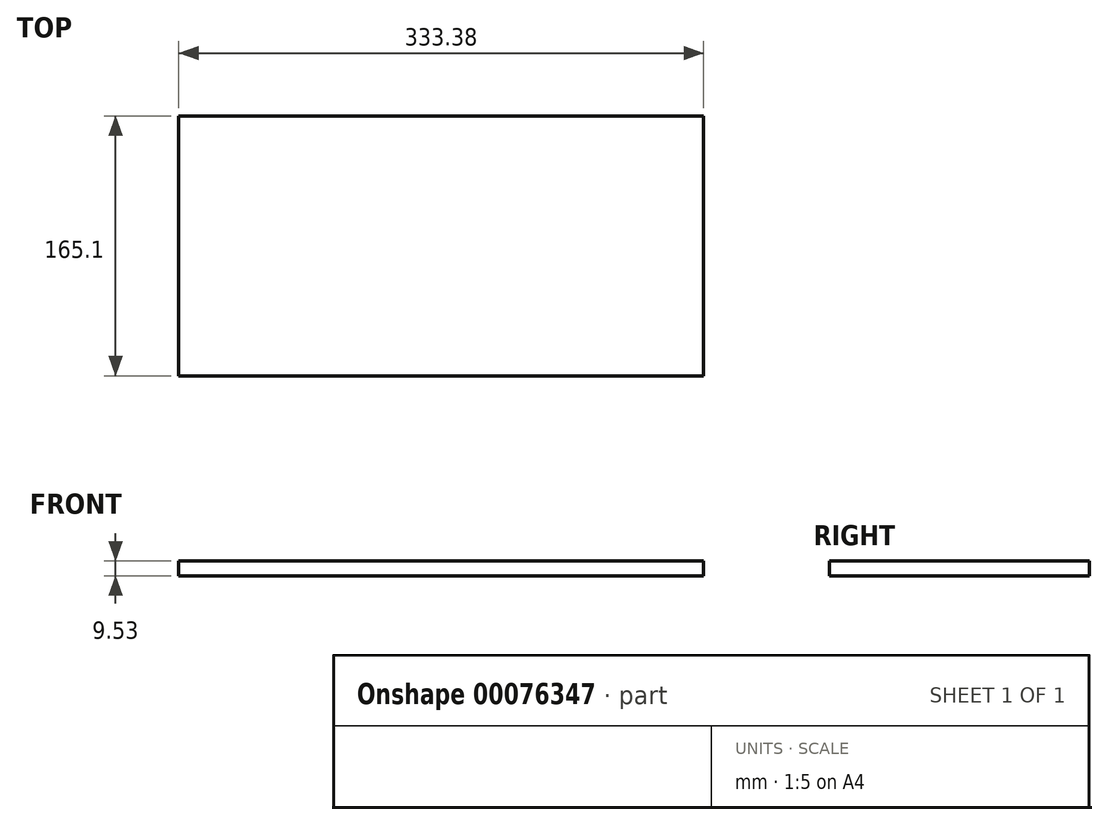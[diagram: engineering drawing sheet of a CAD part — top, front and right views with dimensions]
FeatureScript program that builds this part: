
annotation { "Feature Type Name" : "Feature", "Feature Type Description" : "" }
export const myFeature = defineFeature(function(context is Context, id is Id, definition is map)
    precondition{}
    {
        {
            var Q0;
            Q0=qCreatedBy(makeId("Top.planeOp"),FACE);
            var sketch = newSketch(context, id + "F0", { "sketchPlane" : qUnion([Q0])});
            skLineSegment(sketch, "E0.bottom", {"start": v(166.69, 82.55) * mm, "end": v(-166.69, 82.55) * mm});
            skLineSegment(sketch, "E0.top", {"start": v(166.69, -82.55) * mm, "end": v(-166.69, -82.55) * mm});
            skLineSegment(sketch, "E0.left", {"start": v(166.69, 82.55) * mm, "end": v(166.69, -82.55) * mm});
            skLineSegment(sketch, "E0.right", {"start": v(-166.69, 82.55) * mm, "end": v(-166.69, -82.55) * mm});
            skPoint(sketch, "E0.middle", {"position": v(0, 0) * mm});
            skSolve(sketch);
        }
        {
            var Q0;
            Q0 = qSketchRegion(id + "F0", true);
            extrude(context, id + "F1", {"entities" : qUnion([Q0]), "depth" : 9.53 * mm});
        }
    });
